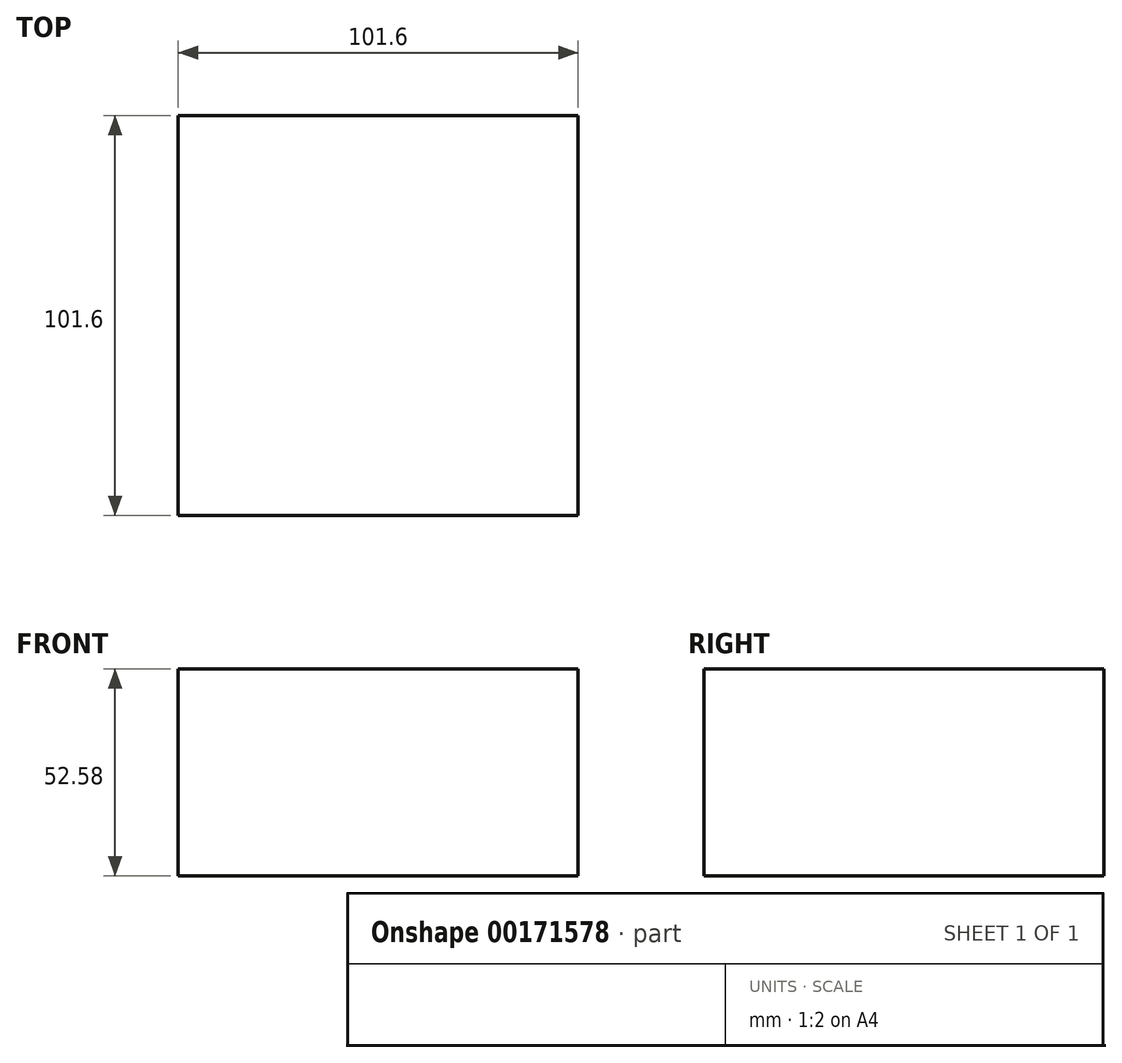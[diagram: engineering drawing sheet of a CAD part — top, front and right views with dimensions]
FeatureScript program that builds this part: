
annotation { "Feature Type Name" : "Feature", "Feature Type Description" : "" }
export const myFeature = defineFeature(function(context is Context, id is Id, definition is map)
    precondition{}
    {
        {
            var Q0;
            Q0=qCreatedBy(makeId("Top.planeOp"),FACE);
            var sketch = newSketch(context, id + "F0", { "sketchPlane" : qUnion([Q0])});
            skLineSegment(sketch, "E0.bottom", {"start": v(50.8, -50.8) * mm, "end": v(-50.8, -50.8) * mm});
            skLineSegment(sketch, "E0.top", {"start": v(50.8, 50.8) * mm, "end": v(-50.8, 50.8) * mm});
            skLineSegment(sketch, "E0.left", {"start": v(50.8, -50.8) * mm, "end": v(50.8, 50.8) * mm});
            skLineSegment(sketch, "E0.right", {"start": v(-50.8, -50.8) * mm, "end": v(-50.8, 50.8) * mm});
            skPoint(sketch, "E0.middle", {"position": v(0, 0) * mm});
            skSolve(sketch);
        }
        {
            var Q0;
            Q0=makeQuery(id+"F0.imprint","IMPRINT",FACE,{"disambiguationData":[TD([[makeQuery(id+"F0.imprint","IMPRINT",EDGE,{"derivedFrom":sQuery(id+"F0.wireOp",EDGE,"E0.bottom")}),-1.0]])]});
            extrude(context, id + "F1", {"entities" : qUnion([Q0]), "depth" : 52.58 * mm});
        }
    });
